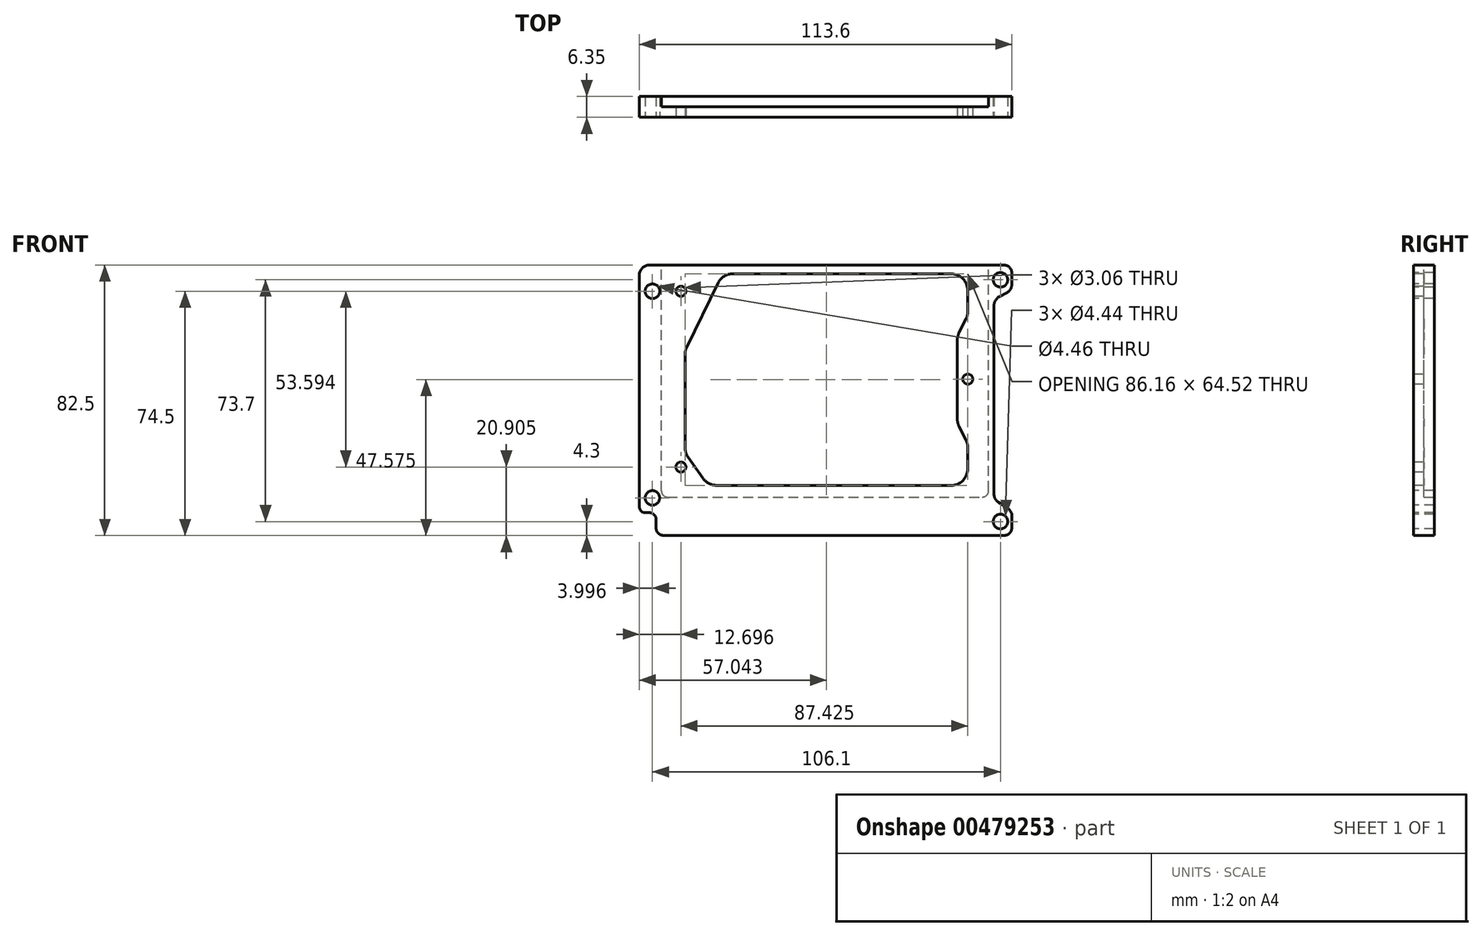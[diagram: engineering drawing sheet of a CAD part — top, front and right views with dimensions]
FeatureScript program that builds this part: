
annotation { "Feature Type Name" : "Feature", "Feature Type Description" : "" }
export const myFeature = defineFeature(function(context is Context, id is Id, definition is map)
    precondition{}
    {
        {
            var Q0;
            Q0=qCreatedBy(makeId("Front.planeOp"),FACE);
            var sketch = newSketch(context, id + "F0", { "sketchPlane" : qUnion([Q0])});
            skLineSegment(sketch, "E0.bottom", {"start": v(-53.62, 41.25) * mm, "end": v(54.27, 41.25) * mm});
            skLineSegment(sketch, "E0.top", {"start": v(-49.17, -41.25) * mm, "end": v(54.27, -41.25) * mm});
            skLineSegment(sketch, "E0.left", {"start": v(-56.8, 38.07) * mm, "end": v(-56.8, -32.36) * mm});
            skLineSegment(sketch, "E0.right", {"start": v(56.8, 38.7) * mm, "end": v(56.8, 35.54) * mm});
            skLineSegment(sketch, "E1.right", {"start": v(51.3, 28.81) * mm, "end": v(51.3, -28.46) * mm});
            skLineSegment(sketch, "E2", {"start": v(53, 31.62) * mm, "end": v(55.11, 32.74) * mm});
            skLineSegment(sketch, "E3", {"start": v(52.81, -31.16) * mm, "end": v(55.3, -32.7) * mm});
            skLineSegment(sketch, "E4.trimOffspring", {"start": v(56.8, -35.4) * mm, "end": v(56.8, -38.71) * mm});
            skLineSegment(sketch, "E5.top", {"start": v(-54.89, -34.27) * mm, "end": v(-53.62, -34.27) * mm});
            skLineSegment(sketch, "E5.right", {"start": v(-51.71, -38.71) * mm, "end": v(-51.71, -36.17) * mm});
            skPoint(sketch, "E6", {"position": v(-52.8, 33.25) * mm});
            skPoint(sketch, "E7", {"position": v(-52.8, -29.75) * mm});
            skPoint(sketch, "E8", {"position": v(53.3, 36.75) * mm});
            skPoint(sketch, "E9", {"position": v(53.3, -36.95) * mm});
            skPoint(sketch, "E10.visualSharp", {"position": v(-56.8, 41.25) * mm});
            skArc(sketch, "E10.filletArc", {"start": v(-53.62, 41.25) * mm, "mid": v(-55.86, 40.32) * mm, "end": v(-56.8, 38.07) * mm});
            skPoint(sketch, "E11.visualSharp", {"position": v(56.8, 41.25) * mm});
            skArc(sketch, "E11.filletArc", {"start": v(56.8, 38.7) * mm, "mid": v(56.06, 40.5) * mm, "end": v(54.27, 41.25) * mm});
            skPoint(sketch, "E12.visualSharp", {"position": v(56.8, -41.25) * mm});
            skArc(sketch, "E12.filletArc", {"start": v(54.27, -41.25) * mm, "mid": v(56.06, -40.5) * mm, "end": v(56.8, -38.71) * mm});
            skPoint(sketch, "E13.visualSharp", {"position": v(-51.71, -41.25) * mm});
            skArc(sketch, "E13.filletArc", {"start": v(-51.71, -38.71) * mm, "mid": v(-50.97, -40.5) * mm, "end": v(-49.17, -41.25) * mm});
            skPoint(sketch, "E14.visualSharp", {"position": v(51.3, -30.23) * mm});
            skArc(sketch, "E14.filletArc", {"start": v(51.3, -28.46) * mm, "mid": v(51.7, -30) * mm, "end": v(52.81, -31.16) * mm});
            skPoint(sketch, "E15.visualSharp", {"position": v(51.3, 30.73) * mm});
            skArc(sketch, "E15.filletArc", {"start": v(53, 31.62) * mm, "mid": v(51.76, 30.45) * mm, "end": v(51.3, 28.81) * mm});
            skPoint(sketch, "E16.visualSharp", {"position": v(56.8, 33.63) * mm});
            skArc(sketch, "E16.filletArc", {"start": v(55.11, 32.74) * mm, "mid": v(56.35, 33.9) * mm, "end": v(56.8, 35.54) * mm});
            skPoint(sketch, "E17.visualSharp", {"position": v(56.8, -33.63) * mm});
            skArc(sketch, "E17.filletArc", {"start": v(56.8, -35.4) * mm, "mid": v(56.4, -33.85) * mm, "end": v(55.3, -32.7) * mm});
            skPoint(sketch, "E18.visualSharp", {"position": v(-56.8, -34.27) * mm});
            skArc(sketch, "E18.filletArc", {"start": v(-56.8, -32.36) * mm, "mid": v(-56.24, -33.7) * mm, "end": v(-54.89, -34.27) * mm});
            skPoint(sketch, "E19.visualSharp", {"position": v(-51.71, -34.27) * mm});
            skCircle(sketch, "E20", {"center": v(53.3, 36.75) * mm, "radius": 2.22 * mm});
            skCircle(sketch, "E21", {"center": v(53.3, -36.95) * mm, "radius": 2.22 * mm});
            skCircle(sketch, "E22", {"center": v(-52.8, -29.75) * mm, "radius": 2.22 * mm});
            skCircle(sketch, "E23", {"center": v(-52.8, 33.25) * mm, "radius": 2.23 * mm});
            skPoint(sketch, "E24", {"position": v(-44.1, 33.25) * mm});
            skPoint(sketch, "E25", {"position": v(-44.1, -20.35) * mm});
            skPoint(sketch, "E26", {"position": v(43.33, 6.45) * mm});
            skCircle(sketch, "E27", {"center": v(-44.1, -20.35) * mm, "radius": 1.53 * mm});
            skCircle(sketch, "E28", {"center": v(-44.1, 33.25) * mm, "radius": 1.53 * mm});
            skCircle(sketch, "E29", {"center": v(43.33, 6.45) * mm, "radius": 1.53 * mm});
            skLineSegment(sketch, "E30", {"start": v(38.25, -25.93) * mm, "end": v(-33.2, -25.93) * mm});
            skLineSegment(sketch, "E31", {"start": v(-42.82, -14.42) * mm, "end": v(-42.82, 14.04) * mm});
            skLineSegment(sketch, "E32", {"start": v(-37.36, -23.78) * mm, "end": v(-41.9, -17.34) * mm});
            skLineSegment(sketch, "E33", {"start": v(38.25, 38.58) * mm, "end": v(-28.22, 38.58) * mm});
            skLineSegment(sketch, "E34", {"start": v(-42.3, 16.27) * mm, "end": v(-32.79, 35.73) * mm});
            skLineSegment(sketch, "E35", {"start": v(43.33, 6.45) * mm, "end": v(43.33, 7.98) * mm});
            skLineSegment(sketch, "E36", {"start": v(43.33, 6.45) * mm, "end": v(43.33, 4.92) * mm});
            skLineSegment(sketch, "E37", {"start": v(40.16, -5.68) * mm, "end": v(40.16, 18.33) * mm});
            skLineSegment(sketch, "E38", {"start": v(42.8, 24.8) * mm, "end": v(40.7, 20.6) * mm});
            skLineSegment(sketch, "E39", {"start": v(42.8, -12.16) * mm, "end": v(40.7, -7.96) * mm});
            skLineSegment(sketch, "E40.trimOffspring", {"start": v(43.33, -14.43) * mm, "end": v(43.33, -20.85) * mm});
            skLineSegment(sketch, "E41.trimOffspring", {"start": v(43.33, 27.08) * mm, "end": v(43.33, 33.5) * mm});
            skPoint(sketch, "E42.visualSharp", {"position": v(-35.84, -25.93) * mm});
            skArc(sketch, "E42.filletArc", {"start": v(-37.36, -23.78) * mm, "mid": v(-35.54, -25.36) * mm, "end": v(-33.2, -25.93) * mm});
            skPoint(sketch, "E43.visualSharp", {"position": v(-42.82, -16.03) * mm});
            skArc(sketch, "E43.filletArc", {"start": v(-42.82, -14.42) * mm, "mid": v(-42.59, -15.95) * mm, "end": v(-41.9, -17.34) * mm});
            skPoint(sketch, "E44.visualSharp", {"position": v(-42.82, 15.21) * mm});
            skArc(sketch, "E44.filletArc", {"start": v(-42.3, 16.27) * mm, "mid": v(-42.7, 15.18) * mm, "end": v(-42.82, 14.04) * mm});
            skPoint(sketch, "E45.visualSharp", {"position": v(-31.4, 38.58) * mm});
            skArc(sketch, "E45.filletArc", {"start": v(-28.22, 38.58) * mm, "mid": v(-30.91, 37.81) * mm, "end": v(-32.79, 35.73) * mm});
            skPoint(sketch, "E46.visualSharp", {"position": v(43.33, 38.58) * mm});
            skArc(sketch, "E46.filletArc", {"start": v(43.33, 33.5) * mm, "mid": v(41.84, 37.1) * mm, "end": v(38.25, 38.58) * mm});
            skPoint(sketch, "E47.visualSharp", {"position": v(43.33, 25.88) * mm});
            skArc(sketch, "E47.filletArc", {"start": v(42.8, 24.8) * mm, "mid": v(43.2, 25.91) * mm, "end": v(43.33, 27.08) * mm});
            skPoint(sketch, "E48.visualSharp", {"position": v(40.16, 19.53) * mm});
            skArc(sketch, "E48.filletArc", {"start": v(40.7, 20.6) * mm, "mid": v(40.3, 19.5) * mm, "end": v(40.16, 18.33) * mm});
            skPoint(sketch, "E49.visualSharp", {"position": v(40.16, -6.88) * mm});
            skArc(sketch, "E49.filletArc", {"start": v(40.16, -5.68) * mm, "mid": v(40.3, -6.85) * mm, "end": v(40.7, -7.96) * mm});
            skPoint(sketch, "E50.visualSharp", {"position": v(43.33, -13.23) * mm});
            skArc(sketch, "E50.filletArc", {"start": v(43.33, -14.43) * mm, "mid": v(43.2, -13.27) * mm, "end": v(42.8, -12.16) * mm});
            skPoint(sketch, "E51.visualSharp", {"position": v(43.33, -25.93) * mm});
            skArc(sketch, "E51.filletArc", {"start": v(38.25, -25.93) * mm, "mid": v(41.84, -24.45) * mm, "end": v(43.33, -20.85) * mm});
            skArc(sketch, "E52.filletArc", {"start": v(-51.71, -36.17) * mm, "mid": v(-52.27, -34.82) * mm, "end": v(-53.62, -34.27) * mm});
            skSolve(sketch);
        }
        {
            var Q0;
            Q0=makeQuery(id+"F0.imprint","IMPRINT",FACE,{"disambiguationData":[TD([[makeQuery(id+"F0.imprint","IMPRINT",EDGE,{"derivedFrom":sQuery(id+"F0.wireOp",EDGE,"E0.bottom")}),-1.0]])]});
            extrude(context, id + "F1", {"entities" : qUnion([Q0]), "oppositeDirection" : true, "depth" : 6.35 * mm, "offsetDistance" : 25.4 * mm});
        }
        {
            var Q0;
            Q0=makeQuery(id+"F1.opExtrude","CAP_FACE",FACE,{"disambiguationData":[OSD([sQuery(id+"F0.wireOp",EDGE,"E0.bottom"),sQuery(id+"F0.wireOp",EDGE,"E0.top"),sQuery(id+"F0.wireOp",EDGE,"E0.left"),sQuery(id+"F0.wireOp",EDGE,"E0.right"),sQuery(id+"F0.wireOp",EDGE,"E1.right"),sQuery(id+"F0.wireOp",EDGE,"E2"),sQuery(id+"F0.wireOp",EDGE,"E3"),sQuery(id+"F0.wireOp",EDGE,"E4.trimOffspring"),sQuery(id+"F0.wireOp",EDGE,"E5.top"),sQuery(id+"F0.wireOp",EDGE,"E5.right"),sQuery(id+"F0.wireOp",EDGE,"E10.filletArc"),sQuery(id+"F0.wireOp",EDGE,"E11.filletArc"),sQuery(id+"F0.wireOp",EDGE,"E12.filletArc"),sQuery(id+"F0.wireOp",EDGE,"E13.filletArc"),sQuery(id+"F0.wireOp",EDGE,"E14.filletArc"),sQuery(id+"F0.wireOp",EDGE,"E15.filletArc"),sQuery(id+"F0.wireOp",EDGE,"E16.filletArc"),sQuery(id+"F0.wireOp",EDGE,"E17.filletArc"),sQuery(id+"F0.wireOp",EDGE,"E18.filletArc"),sQuery(id+"F0.wireOp",EDGE,"E20"),sQuery(id+"F0.wireOp",EDGE,"E21"),sQuery(id+"F0.wireOp",EDGE,"E22"),sQuery(id+"F0.wireOp",EDGE,"E23"),sQuery(id+"F0.wireOp",EDGE,"E27"),sQuery(id+"F0.wireOp",EDGE,"E28"),sQuery(id+"F0.wireOp",EDGE,"E29"),sQuery(id+"F0.wireOp",EDGE,"E30"),sQuery(id+"F0.wireOp",EDGE,"E31"),sQuery(id+"F0.wireOp",EDGE,"E32"),sQuery(id+"F0.wireOp",EDGE,"E33"),sQuery(id+"F0.wireOp",EDGE,"E34"),sQuery(id+"F0.wireOp",EDGE,"E37"),sQuery(id+"F0.wireOp",EDGE,"E38"),sQuery(id+"F0.wireOp",EDGE,"E39"),sQuery(id+"F0.wireOp",EDGE,"E40.trimOffspring"),sQuery(id+"F0.wireOp",EDGE,"E41.trimOffspring"),sQuery(id+"F0.wireOp",EDGE,"E42.filletArc"),sQuery(id+"F0.wireOp",EDGE,"E43.filletArc"),sQuery(id+"F0.wireOp",EDGE,"E44.filletArc"),sQuery(id+"F0.wireOp",EDGE,"E45.filletArc"),sQuery(id+"F0.wireOp",EDGE,"E46.filletArc"),sQuery(id+"F0.wireOp",EDGE,"E47.filletArc"),sQuery(id+"F0.wireOp",EDGE,"E48.filletArc"),sQuery(id+"F0.wireOp",EDGE,"E49.filletArc"),sQuery(id+"F0.wireOp",EDGE,"E50.filletArc"),sQuery(id+"F0.wireOp",EDGE,"E51.filletArc")])],"isStart":false});
            var sketch = newSketch(context, id + "F2", { "sketchPlane" : qUnion([Q0])});
            skLineSegment(sketch, "E53", {"start": v(48.16, -29.49) * mm, "end": v(-47.78, -29.49) * mm});
            skLineSegment(sketch, "E54", {"start": v(50.06, 41.38) * mm, "end": v(-49.68, 41.38) * mm});
            skPoint(sketch, "E55", {"position": v(44.1, -20.35) * mm});
            skPoint(sketch, "E56", {"position": v(44.1, 33.25) * mm});
            skPoint(sketch, "E57", {"position": v(-43.33, 6.45) * mm});
            skLineSegment(sketch, "E58", {"start": v(50.06, -27.58) * mm, "end": v(50.06, 41.38) * mm});
            skLineSegment(sketch, "E59", {"start": v(-49.68, -27.58) * mm, "end": v(-49.68, 41.38) * mm});
            skPoint(sketch, "E60.visualSharp", {"position": v(50.06, -29.49) * mm});
            skArc(sketch, "E60.filletArc", {"start": v(48.16, -29.49) * mm, "mid": v(49.5, -28.93) * mm, "end": v(50.06, -27.58) * mm});
            skPoint(sketch, "E61.visualSharp", {"position": v(-49.68, -29.49) * mm});
            skArc(sketch, "E61.filletArc", {"start": v(-49.68, -27.58) * mm, "mid": v(-49.12, -28.93) * mm, "end": v(-47.78, -29.49) * mm});
            skSolve(sketch);
        }
        {
            var Q0;
            Q0=makeQuery(id+"F2.imprint","IMPRINT",FACE,{"disambiguationData":[TD([[makeQuery(id+"F2.imprint","IMPRINT",EDGE,{"derivedFrom":sQuery(id+"F2.wireOp",EDGE,"E53")}),-1.0]])]});
            extrude(context, id + "F3", {"entities" : qUnion([Q0]), "operationType" : NewBodyOperationType.REMOVE, "oppositeDirection" : true, "depth" : 3.17 * mm, "offsetDistance" : 25.4 * mm});
        }
    });
